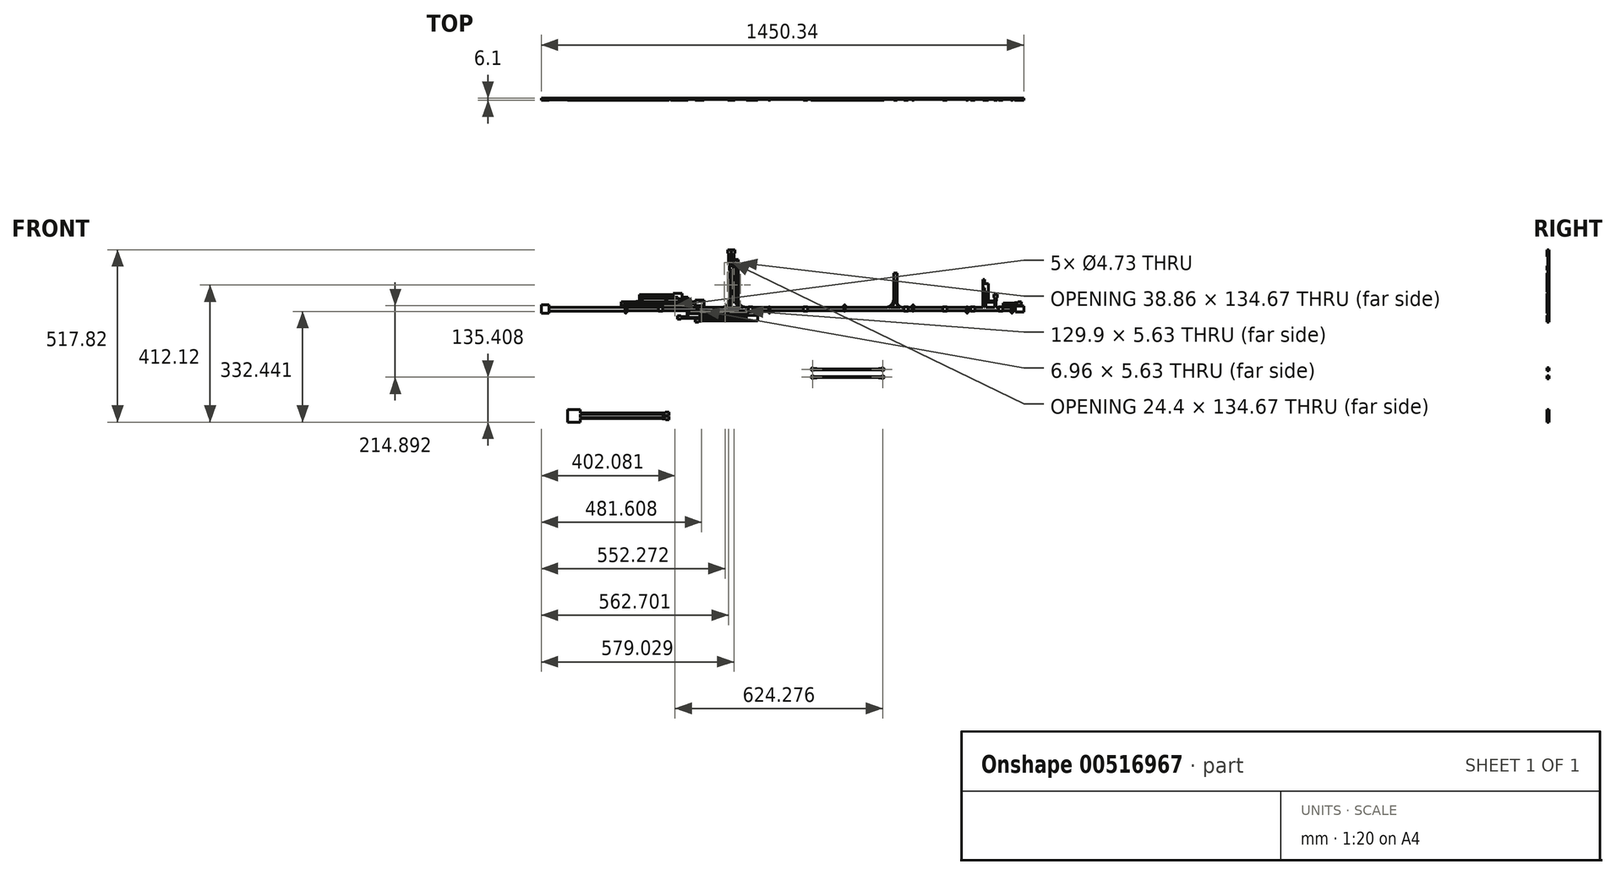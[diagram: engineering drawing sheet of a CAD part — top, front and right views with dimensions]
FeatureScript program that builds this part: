
annotation { "Feature Type Name" : "Feature", "Feature Type Description" : "" }
export const myFeature = defineFeature(function(context is Context, id is Id, definition is map)
    precondition{}
    {
        {
            var Q0;
            Q0=qCreatedBy(makeId("Front.planeOp"),FACE);
            var sketch = newSketch(context, id + "F0", { "sketchPlane" : qUnion([Q0])});
            skLineSegment(sketch, "E0.bottom", {"start": v(-1284.8, 12.7) * mm, "end": v(-1261.94, 12.7) * mm});
            skLineSegment(sketch, "E0.top", {"start": v(-1284.8, -12.7) * mm, "end": v(-1261.94, -12.7) * mm});
            skLineSegment(sketch, "E0.left", {"start": v(-1284.8, 12.7) * mm, "end": v(-1284.8, -12.7) * mm});
            skLineSegment(sketch, "E0.right", {"start": v(-1261.94, 12.7) * mm, "end": v(-1261.94, -12.7) * mm});
            skPoint(sketch, "E0.middle", {"position": v(-1273.37, 0) * mm});
            skLineSegment(sketch, "E1", {"start": v(-1273.37, 0) * mm, "end": v(152.84, 0) * mm, "construction": true});
            skLineSegment(sketch, "E2.bottom", {"start": v(140.14, 8.38) * mm, "end": v(165.54, 8.38) * mm});
            skLineSegment(sketch, "E2.top", {"start": v(140.14, -8.38) * mm, "end": v(165.54, -8.38) * mm});
            skLineSegment(sketch, "E2.left", {"start": v(140.14, 8.38) * mm, "end": v(140.14, -8.38) * mm});
            skLineSegment(sketch, "E2.right", {"start": v(165.54, 8.38) * mm, "end": v(165.54, -8.38) * mm});
            skPoint(sketch, "E2.middle", {"position": v(152.84, 0) * mm});
            skLineSegment(sketch, "E3.bottom", {"start": v(-795.85, 9.73) * mm, "end": v(-822.52, 9.73) * mm});
            skLineSegment(sketch, "E3.top", {"start": v(-795.85, 26.5) * mm, "end": v(-822.52, 26.5) * mm});
            skLineSegment(sketch, "E3.left", {"start": v(-795.85, 9.73) * mm, "end": v(-795.85, 26.5) * mm});
            skLineSegment(sketch, "E3.right", {"start": v(-822.52, 9.73) * mm, "end": v(-822.52, 26.5) * mm});
            skPoint(sketch, "E3.middle", {"position": v(-809.19, 18.11) * mm});
            skLineSegment(sketch, "E4.bottom", {"start": v(-861.64, 35.7) * mm, "end": v(-888.05, 35.7) * mm});
            skLineSegment(sketch, "E4.top", {"start": v(-861.64, 47.38) * mm, "end": v(-888.05, 47.38) * mm});
            skLineSegment(sketch, "E4.left", {"start": v(-861.64, 35.7) * mm, "end": v(-861.64, 47.38) * mm});
            skLineSegment(sketch, "E4.right", {"start": v(-888.05, 35.7) * mm, "end": v(-888.05, 47.38) * mm});
            skPoint(sketch, "E4.middle", {"position": v(-874.85, 41.54) * mm});
            skLineSegment(sketch, "E5.bottom", {"start": v(-874.08, 35.7) * mm, "end": v(-844.11, 35.7) * mm});
            skLineSegment(sketch, "E5.top", {"start": v(-874.08, 30.62) * mm, "end": v(-844.11, 30.62) * mm});
            skLineSegment(sketch, "E5.left", {"start": v(-874.08, 35.7) * mm, "end": v(-874.08, 30.62) * mm});
            skLineSegment(sketch, "E5.right", {"start": v(-844.11, 35.7) * mm, "end": v(-844.11, 30.62) * mm});
            skArc(sketch, "E6", {"start": v(-886.53, 8.25) * mm, "mid": v(-878.4, 10.28) * mm, "end": v(-886.53, 12.31) * mm});
            skCircle(sketch, "E7", {"center": v(-882.72, 10.28) * mm, "radius": 2.36 * mm});
            skLineSegment(sketch, "E8.bottom", {"start": v(-886.53, 12.31) * mm, "end": v(-895.17, 12.31) * mm});
            skLineSegment(sketch, "E8.top", {"start": v(-886.53, 8.25) * mm, "end": v(-895.17, 8.25) * mm});
            skLineSegment(sketch, "E8.right", {"start": v(-895.17, 12.31) * mm, "end": v(-895.17, 8.25) * mm});
            skLineSegment(sketch, "E9.bottom", {"start": v(-1032.58, 6.35) * mm, "end": v(-1029.02, 6.35) * mm});
            skLineSegment(sketch, "E9.top", {"start": v(-1032.61, -6.35) * mm, "end": v(-1029.06, -6.35) * mm});
            skLineSegment(sketch, "E9.right", {"start": v(-1029.02, 6.35) * mm, "end": v(-1029.06, -6.35) * mm});
            skPoint(sketch, "E9.middle", {"position": v(-1030.82, 0) * mm});
            skLineSegment(sketch, "E10", {"start": v(-1032.58, 6.35) * mm, "end": v(-1032.61, -6.35) * mm});
            skCircle(sketch, "E11", {"center": v(-1030.83, -8.98) * mm, "radius": 3.18 * mm});
            skPoint(sketch, "E12", {"position": v(-1030.8, 6.35) * mm});
            skPoint(sketch, "E13", {"position": v(-895.17, 10.28) * mm});
            skLineSegment(sketch, "E14", {"start": v(-1261.94, 6.35) * mm, "end": v(140.14, 6.35) * mm, "construction": true});
            skLineSegment(sketch, "E15", {"start": v(-1261.94, -6.35) * mm, "end": v(140.14, -6.35) * mm, "construction": true});
            skLineSegment(sketch, "E16", {"start": v(-1240.29, 6.35) * mm, "end": v(-1240.29, -6.35) * mm, "construction": true});
            skPoint(sketch, "E17", {"position": v(-1240.29, 0) * mm});
            skLineSegment(sketch, "E18.bottom", {"start": v(-932, 6.35) * mm, "end": v(-919.3, 6.35) * mm});
            skLineSegment(sketch, "E18.top", {"start": v(-932, -6.35) * mm, "end": v(-919.3, -6.35) * mm});
            skLineSegment(sketch, "E18.left", {"start": v(-932, 6.35) * mm, "end": v(-932, -6.35) * mm});
            skLineSegment(sketch, "E18.right", {"start": v(-919.3, 6.35) * mm, "end": v(-919.3, -6.35) * mm});
            skLineSegment(sketch, "E19.right", {"start": v(-813.12, 6.35) * mm, "end": v(-813.12, -6.35) * mm});
            skLineSegment(sketch, "E20", {"start": v(-816.68, 6.35) * mm, "end": v(-816.68, -6.35) * mm});
            skCircle(sketch, "E21", {"center": v(-814.9, -8.98) * mm, "radius": 3.18 * mm});
            skLineSegment(sketch, "E22", {"start": v(-813.12, 6.35) * mm, "end": v(-816.68, 6.35) * mm});
            skPoint(sketch, "E23", {"position": v(-814.9, 6.35) * mm});
            skLineSegment(sketch, "E24.1.0.0", {"start": v(-600.78, 6.35) * mm, "end": v(-600.78, -6.35) * mm});
            skLineSegment(sketch, "E24.1.0.1", {"start": v(-597.22, 6.35) * mm, "end": v(-597.22, -6.35) * mm});
            skCircle(sketch, "E24.1.0.2", {"center": v(-599, -8.98) * mm, "radius": 3.18 * mm});
            skLineSegment(sketch, "E24.direction1", {"start": v(-814.9, -8.98) * mm, "end": v(-599, -8.98) * mm, "construction": true});
            skLineSegment(sketch, "E25", {"start": v(-600.78, 6.35) * mm, "end": v(-597.22, 6.35) * mm});
            skLineSegment(sketch, "E26.bottom", {"start": v(-668.6, -19.14) * mm, "end": v(-634.56, -19.14) * mm});
            skLineSegment(sketch, "E26.top", {"start": v(-668.6, -34.89) * mm, "end": v(-634.56, -34.89) * mm});
            skLineSegment(sketch, "E26.left", {"start": v(-668.6, -19.14) * mm, "end": v(-668.6, -34.89) * mm});
            skLineSegment(sketch, "E26.right", {"start": v(-634.56, -19.14) * mm, "end": v(-634.56, -34.89) * mm});
            skLineSegment(sketch, "E27.bottom", {"start": v(-822.52, -28.63) * mm, "end": v(-812.36, -28.63) * mm});
            skLineSegment(sketch, "E27.top", {"start": v(-822.52, -38.79) * mm, "end": v(-812.36, -38.79) * mm});
            skLineSegment(sketch, "E27.left", {"start": v(-822.52, -28.63) * mm, "end": v(-822.52, -38.79) * mm});
            skLineSegment(sketch, "E27.right", {"start": v(-812.36, -28.63) * mm, "end": v(-812.36, -38.79) * mm});
            skLineSegment(sketch, "E28.bottom", {"start": v(-812.36, -31.17) * mm, "end": v(-802.2, -31.17) * mm});
            skLineSegment(sketch, "E28.top", {"start": v(-812.36, -36.25) * mm, "end": v(-802.2, -36.25) * mm});
            skLineSegment(sketch, "E28.left", {"start": v(-812.36, -31.17) * mm, "end": v(-812.36, -36.25) * mm});
            skLineSegment(sketch, "E28.right", {"start": v(-802.2, -31.17) * mm, "end": v(-802.2, -36.25) * mm});
            skPoint(sketch, "E29", {"position": v(-812.36, -33.7) * mm});
            skLineSegment(sketch, "E30.bottom", {"start": v(-875.86, -19.87) * mm, "end": v(-865.7, -19.87) * mm});
            skLineSegment(sketch, "E30.top", {"start": v(-875.86, -30.03) * mm, "end": v(-865.7, -30.03) * mm});
            skLineSegment(sketch, "E30.left", {"start": v(-875.86, -19.87) * mm, "end": v(-875.86, -30.03) * mm});
            skLineSegment(sketch, "E30.right", {"start": v(-865.7, -19.87) * mm, "end": v(-865.7, -30.03) * mm});
            skLineSegment(sketch, "E31.bottom", {"start": v(-865.7, -22.41) * mm, "end": v(-855.54, -22.41) * mm});
            skLineSegment(sketch, "E31.top", {"start": v(-865.7, -27.5) * mm, "end": v(-855.54, -27.5) * mm});
            skLineSegment(sketch, "E31.left", {"start": v(-865.7, -22.41) * mm, "end": v(-865.7, -27.5) * mm});
            skLineSegment(sketch, "E31.right", {"start": v(-855.54, -22.41) * mm, "end": v(-855.54, -27.5) * mm});
            skPoint(sketch, "E32", {"position": v(-865.7, -24.95) * mm});
            skLineSegment(sketch, "E33.bottom", {"start": v(-662.5, 6.35) * mm, "end": v(-649.8, 6.35) * mm});
            skLineSegment(sketch, "E33.top", {"start": v(-662.5, -8.98) * mm, "end": v(-649.8, -8.98) * mm});
            skLineSegment(sketch, "E33.left", {"start": v(-662.5, 6.35) * mm, "end": v(-662.5, -8.98) * mm});
            skLineSegment(sketch, "E33.right", {"start": v(-649.8, 6.35) * mm, "end": v(-649.8, -8.98) * mm});
            skPoint(sketch, "E34", {"position": v(-599, 6.35) * mm});
            skLineSegment(sketch, "E35.bottom", {"start": v(-724.32, 177.8) * mm, "end": v(-714.16, 177.8) * mm});
            skLineSegment(sketch, "E35.top", {"start": v(-724.32, 167.64) * mm, "end": v(-714.16, 167.64) * mm});
            skLineSegment(sketch, "E35.left", {"start": v(-724.32, 177.8) * mm, "end": v(-724.32, 167.64) * mm});
            skLineSegment(sketch, "E35.right", {"start": v(-714.16, 177.8) * mm, "end": v(-714.16, 167.64) * mm});
            skLineSegment(sketch, "E36.bottom", {"start": v(-716.7, 167.64) * mm, "end": v(-721.78, 167.64) * mm});
            skLineSegment(sketch, "E36.top", {"start": v(-716.7, 157.48) * mm, "end": v(-721.78, 157.48) * mm});
            skLineSegment(sketch, "E36.left", {"start": v(-716.7, 167.64) * mm, "end": v(-716.7, 157.48) * mm});
            skLineSegment(sketch, "E36.right", {"start": v(-721.78, 167.64) * mm, "end": v(-721.78, 157.48) * mm});
            skPoint(sketch, "E37", {"position": v(-719.24, 167.64) * mm});
            skLineSegment(sketch, "E38", {"start": v(-713.3, 0) * mm, "end": v(-713.3, 177.8) * mm, "construction": true});
            skLineSegment(sketch, "E39.MirrorCS", {"start": v(-702.28, 167.64) * mm, "end": v(-712.44, 167.64) * mm});
            skLineSegment(sketch, "E40.MirrorCS", {"start": v(-709.9, 167.64) * mm, "end": v(-704.82, 167.64) * mm});
            skPoint(sketch, "E41.MirrorP", {"position": v(-707.36, 167.64) * mm});
            skLineSegment(sketch, "E42.MirrorCS", {"start": v(-712.44, 177.8) * mm, "end": v(-712.44, 167.64) * mm});
            skLineSegment(sketch, "E43.MirrorCS", {"start": v(-702.28, 177.8) * mm, "end": v(-712.44, 177.8) * mm});
            skLineSegment(sketch, "E44.MirrorCS", {"start": v(-709.9, 157.48) * mm, "end": v(-704.82, 157.48) * mm});
            skLineSegment(sketch, "E45.MirrorCS", {"start": v(-702.28, 177.8) * mm, "end": v(-702.28, 167.64) * mm});
            skLineSegment(sketch, "E46.MirrorCS", {"start": v(-709.9, 167.64) * mm, "end": v(-709.9, 157.48) * mm});
            skLineSegment(sketch, "E47.MirrorCS", {"start": v(-704.82, 167.64) * mm, "end": v(-704.82, 157.48) * mm});
            skLineSegment(sketch, "E48.bottom", {"start": v(-719.65, 130.18) * mm, "end": v(-706.95, 130.18) * mm});
            skLineSegment(sketch, "E48.top", {"start": v(-719.65, 117.48) * mm, "end": v(-706.95, 117.48) * mm});
            skLineSegment(sketch, "E48.left", {"start": v(-719.65, 130.18) * mm, "end": v(-719.65, 117.48) * mm});
            skLineSegment(sketch, "E48.right", {"start": v(-706.95, 130.18) * mm, "end": v(-706.95, 117.48) * mm});
            skPoint(sketch, "E49", {"position": v(-713.3, 117.48) * mm});
            skLineSegment(sketch, "E50.bottom", {"start": v(-716.7, 157.48) * mm, "end": v(-719.65, 157.48) * mm});
            skLineSegment(sketch, "E50.top", {"start": v(-716.7, 100.8) * mm, "end": v(-719.65, 100.8) * mm, "construction": true});
            skLineSegment(sketch, "E50.left", {"start": v(-716.7, 157.48) * mm, "end": v(-716.7, 100.8) * mm, "construction": true});
            skLineSegment(sketch, "E50.right", {"start": v(-719.65, 157.48) * mm, "end": v(-719.65, 100.8) * mm, "construction": true});
            skLineSegment(sketch, "E51.bottom", {"start": v(-709.9, 157.48) * mm, "end": v(-706.95, 157.48) * mm});
            skLineSegment(sketch, "E51.top", {"start": v(-709.9, 98.87) * mm, "end": v(-706.95, 98.87) * mm, "construction": true});
            skLineSegment(sketch, "E51.left", {"start": v(-709.9, 157.48) * mm, "end": v(-709.9, 98.87) * mm, "construction": true});
            skLineSegment(sketch, "E51.right", {"start": v(-706.95, 157.48) * mm, "end": v(-706.95, 98.87) * mm, "construction": true});
            skLineSegment(sketch, "E52.1.0.0", {"start": v(-374.72, 6.35) * mm, "end": v(-374.72, -6.35) * mm});
            skLineSegment(sketch, "E52.1.0.1", {"start": v(-371.16, 6.35) * mm, "end": v(-371.16, -6.35) * mm});
            skLineSegment(sketch, "E52.direction1", {"start": v(-599, -8.98) * mm, "end": v(-372.94, -8.98) * mm, "construction": true});
            skLineSegment(sketch, "E53", {"start": v(-374.72, 6.35) * mm, "end": v(-371.16, 6.35) * mm});
            skLineSegment(sketch, "E54.bottom", {"start": v(-497.4, 6.35) * mm, "end": v(-484.7, 6.35) * mm});
            skLineSegment(sketch, "E54.top", {"start": v(-497.4, -6.35) * mm, "end": v(-484.7, -6.35) * mm});
            skLineSegment(sketch, "E54.left", {"start": v(-497.4, 6.35) * mm, "end": v(-497.4, -6.35) * mm});
            skLineSegment(sketch, "E54.right", {"start": v(-484.7, 6.35) * mm, "end": v(-484.7, -6.35) * mm});
            skLineSegment(sketch, "E55.1.0.0", {"start": v(-168.98, 6.35) * mm, "end": v(-168.98, -6.35) * mm});
            skLineSegment(sketch, "E55.1.0.1", {"start": v(-165.42, 6.35) * mm, "end": v(-165.42, -6.35) * mm});
            skLineSegment(sketch, "E55.direction1", {"start": v(-372.94, -8.98) * mm, "end": v(-167.2, -8.98) * mm, "construction": true});
            skLineSegment(sketch, "E56", {"start": v(-168.98, 6.35) * mm, "end": v(-165.42, 6.35) * mm});
            skLineSegment(sketch, "E57.1.0.0", {"start": v(-6.42, 6.35) * mm, "end": v(-6.42, -6.35) * mm});
            skLineSegment(sketch, "E57.1.0.1", {"start": v(-2.86, 6.35) * mm, "end": v(-2.86, -6.35) * mm});
            skCircle(sketch, "E57.1.0.2", {"center": v(-4.64, -8.98) * mm, "radius": 3.18 * mm});
            skLineSegment(sketch, "E57.direction1", {"start": v(-168.98, -6.35) * mm, "end": v(-6.42, -6.35) * mm, "construction": true});
            skLineSegment(sketch, "E58", {"start": v(-6.42, 6.35) * mm, "end": v(-2.86, 6.35) * mm});
            skLineSegment(sketch, "E59.bottom", {"start": v(-195.14, 6.35) * mm, "end": v(-182.44, 6.35) * mm});
            skLineSegment(sketch, "E59.top", {"start": v(-195.14, -6.35) * mm, "end": v(-182.44, -6.35) * mm});
            skLineSegment(sketch, "E59.left", {"start": v(-195.14, 6.35) * mm, "end": v(-195.14, -6.35) * mm});
            skLineSegment(sketch, "E59.right", {"start": v(-182.44, 6.35) * mm, "end": v(-182.44, -6.35) * mm});
            skLineSegment(sketch, "E60.bottom", {"start": v(-78.3, 6.35) * mm, "end": v(-65.6, 6.35) * mm});
            skLineSegment(sketch, "E60.top", {"start": v(-78.3, -6.35) * mm, "end": v(-65.6, -6.35) * mm});
            skLineSegment(sketch, "E60.left", {"start": v(-78.3, 6.35) * mm, "end": v(-78.3, -6.35) * mm});
            skLineSegment(sketch, "E60.right", {"start": v(-65.6, 6.35) * mm, "end": v(-65.6, -6.35) * mm});
            skLineSegment(sketch, "E61.bottom", {"start": v(5.52, 6.35) * mm, "end": v(18.22, 6.35) * mm});
            skLineSegment(sketch, "E61.top", {"start": v(5.52, -6.35) * mm, "end": v(18.22, -6.35) * mm});
            skLineSegment(sketch, "E61.left", {"start": v(5.52, 6.35) * mm, "end": v(5.52, -6.35) * mm});
            skLineSegment(sketch, "E61.right", {"start": v(18.22, 6.35) * mm, "end": v(18.22, -6.35) * mm});
            skLineSegment(sketch, "E62.bottom", {"start": v(89.34, 6.35) * mm, "end": v(102.04, 6.35) * mm});
            skLineSegment(sketch, "E62.top", {"start": v(89.34, -6.35) * mm, "end": v(102.04, -6.35) * mm});
            skLineSegment(sketch, "E62.left", {"start": v(89.34, 6.35) * mm, "end": v(89.34, -6.35) * mm});
            skLineSegment(sketch, "E62.right", {"start": v(102.04, 6.35) * mm, "end": v(102.04, -6.35) * mm});
            skCircle(sketch, "E63.1.0.0", {"center": v(129.98, -8.98) * mm, "radius": 3.18 * mm});
            skLineSegment(sketch, "E63.1.0.1", {"start": v(128.2, 6.35) * mm, "end": v(128.2, -6.35) * mm});
            skLineSegment(sketch, "E63.1.0.2", {"start": v(131.76, 6.35) * mm, "end": v(131.76, -6.35) * mm});
            skLineSegment(sketch, "E63.direction1", {"start": v(-4.64, -8.98) * mm, "end": v(129.98, -8.98) * mm, "construction": true});
            skLineSegment(sketch, "E64", {"start": v(128.2, 6.35) * mm, "end": v(131.76, 6.35) * mm});
            skLineSegment(sketch, "E65", {"start": v(-220.54, 6.35) * mm, "end": v(-220.54, 96.14) * mm, "construction": true});
            skLineSegment(sketch, "E66.bottom", {"start": v(-225.62, 107.95) * mm, "end": v(-215.46, 107.95) * mm});
            skLineSegment(sketch, "E66.top", {"start": v(-225.62, 84.33) * mm, "end": v(-215.46, 84.33) * mm});
            skLineSegment(sketch, "E66.left", {"start": v(-225.62, 107.95) * mm, "end": v(-225.62, 84.33) * mm});
            skLineSegment(sketch, "E66.right", {"start": v(-215.46, 107.95) * mm, "end": v(-215.46, 84.33) * mm});
            skPoint(sketch, "E66.middle", {"position": v(-220.54, 96.14) * mm});
            skLineSegment(sketch, "E67.bottom", {"start": v(147.76, 21.08) * mm, "end": v(157.92, 21.08) * mm});
            skLineSegment(sketch, "E67.top", {"start": v(147.76, 10.92) * mm, "end": v(157.92, 10.92) * mm});
            skLineSegment(sketch, "E67.left", {"start": v(147.76, 21.08) * mm, "end": v(147.76, 10.92) * mm});
            skLineSegment(sketch, "E67.right", {"start": v(157.92, 21.08) * mm, "end": v(157.92, 10.92) * mm});
            skLineSegment(sketch, "E68.bottom", {"start": v(147.76, 18.54) * mm, "end": v(137.6, 18.54) * mm});
            skLineSegment(sketch, "E68.top", {"start": v(147.76, 13.46) * mm, "end": v(137.6, 13.46) * mm});
            skLineSegment(sketch, "E68.left", {"start": v(147.76, 18.54) * mm, "end": v(147.76, 13.46) * mm});
            skLineSegment(sketch, "E68.right", {"start": v(137.6, 18.54) * mm, "end": v(137.6, 13.46) * mm});
            skLineSegment(sketch, "E69.bottom", {"start": v(75.37, 44.45) * mm, "end": v(85.53, 44.45) * mm});
            skLineSegment(sketch, "E69.top", {"start": v(75.37, 34.3) * mm, "end": v(85.53, 34.3) * mm});
            skLineSegment(sketch, "E69.left", {"start": v(75.37, 44.45) * mm, "end": v(75.37, 34.3) * mm});
            skLineSegment(sketch, "E69.right", {"start": v(85.53, 44.45) * mm, "end": v(85.53, 34.3) * mm});
            skLineSegment(sketch, "E70.bottom", {"start": v(77.9, 34.3) * mm, "end": v(82.99, 34.3) * mm});
            skLineSegment(sketch, "E70.top", {"start": v(77.9, 24.13) * mm, "end": v(82.99, 24.13) * mm});
            skLineSegment(sketch, "E70.left", {"start": v(77.9, 34.3) * mm, "end": v(77.9, 24.13) * mm});
            skLineSegment(sketch, "E70.right", {"start": v(82.99, 34.3) * mm, "end": v(82.99, 24.13) * mm});
            skLineSegment(sketch, "E71.bottom", {"start": v(47.43, 76.2) * mm, "end": v(58.86, 76.2) * mm});
            skLineSegment(sketch, "E71.top", {"start": v(47.43, 50.8) * mm, "end": v(58.86, 50.8) * mm});
            skLineSegment(sketch, "E71.left", {"start": v(47.43, 76.2) * mm, "end": v(47.43, 50.8) * mm});
            skLineSegment(sketch, "E71.right", {"start": v(58.86, 76.2) * mm, "end": v(58.86, 50.8) * mm});
            skPoint(sketch, "E72", {"position": v(80.45, 34.3) * mm});
            skPoint(sketch, "E73", {"position": v(147.76, 16) * mm});
            skLineSegment(sketch, "E74.bottom", {"start": v(42.35, 88.9) * mm, "end": v(47.43, 88.9) * mm});
            skLineSegment(sketch, "E74.top", {"start": v(42.35, 63.5) * mm, "end": v(47.43, 63.5) * mm});
            skLineSegment(sketch, "E74.left", {"start": v(42.35, 88.9) * mm, "end": v(42.35, 63.5) * mm});
            skLineSegment(sketch, "E74.right", {"start": v(47.43, 88.9) * mm, "end": v(47.43, 63.5) * mm});
            skCircle(sketch, "E75", {"center": v(-372.94, 8.98) * mm, "radius": 3.18 * mm});
            skLineSegment(sketch, "E76", {"start": v(-374.72, -6.35) * mm, "end": v(-371.16, -6.35) * mm});
            skLineSegment(sketch, "E77", {"start": v(-168.98, -6.35) * mm, "end": v(-165.42, -6.35) * mm});
            skCircle(sketch, "E78", {"center": v(-167.2, 8.98) * mm, "radius": 3.18 * mm});
            skArc(sketch, "E79", {"start": v(-262.25, -183.1) * mm, "mid": v(-254.13, -181.07) * mm, "end": v(-262.25, -179.04) * mm});
            skCircle(sketch, "E80", {"center": v(-258.44, -181.07) * mm, "radius": 2.36 * mm});
            skLineSegment(sketch, "E81.bottom", {"start": v(-262.25, -179.04) * mm, "end": v(-270.89, -179.04) * mm});
            skLineSegment(sketch, "E81.top", {"start": v(-262.25, -183.1) * mm, "end": v(-270.89, -183.1) * mm});
            skLineSegment(sketch, "E81.right", {"start": v(-270.89, -179.04) * mm, "end": v(-270.89, -183.1) * mm});
            skArc(sketch, "E82", {"start": v(-262.25, -206.64) * mm, "mid": v(-254.13, -204.61) * mm, "end": v(-262.25, -202.58) * mm});
            skCircle(sketch, "E83", {"center": v(-258.44, -204.61) * mm, "radius": 2.36 * mm});
            skLineSegment(sketch, "E84.bottom", {"start": v(-262.25, -202.58) * mm, "end": v(-270.89, -202.58) * mm});
            skLineSegment(sketch, "E84.top", {"start": v(-262.25, -206.64) * mm, "end": v(-270.89, -206.64) * mm});
            skLineSegment(sketch, "E84.right", {"start": v(-270.89, -202.58) * mm, "end": v(-270.89, -206.64) * mm});
            skLineSegment(sketch, "E85", {"start": v(-363.85, -66.24) * mm, "end": v(-363.85, -111.75) * mm, "construction": true});
            skLineSegment(sketch, "E86.bottom", {"start": v(-270.89, -182.34) * mm, "end": v(-363.85, -182.34) * mm});
            skLineSegment(sketch, "E86.top", {"start": v(-270.89, -180.49) * mm, "end": v(-363.85, -180.49) * mm});
            skLineSegment(sketch, "E86.left", {"start": v(-270.89, -180.49) * mm, "end": v(-270.89, -182.34) * mm});
            skLineSegment(sketch, "E86.right", {"start": v(-363.85, -180.49) * mm, "end": v(-363.85, -182.34) * mm});
            skLineSegment(sketch, "E87", {"start": v(-270.89, -183.1) * mm, "end": v(-270.89, -202.58) * mm, "construction": true});
            skLineSegment(sketch, "E88", {"start": v(194.55, -192.84) * mm, "end": v(-270.89, -192.84) * mm, "construction": true});
            skLineSegment(sketch, "E89.MirrorCS", {"start": v(-270.89, -205.2) * mm, "end": v(-363.85, -205.2) * mm});
            skLineSegment(sketch, "E90.MirrorCS", {"start": v(-270.89, -203.34) * mm, "end": v(-363.85, -203.34) * mm});
            skLineSegment(sketch, "E91.MirrorCS", {"start": v(-456.82, -179.04) * mm, "end": v(-456.82, -183.1) * mm});
            skLineSegment(sketch, "E92.MirrorCS", {"start": v(-456.82, -180.49) * mm, "end": v(-456.82, -182.34) * mm});
            skLineSegment(sketch, "E93.MirrorCS", {"start": v(-456.82, -202.58) * mm, "end": v(-456.82, -206.64) * mm});
            skLineSegment(sketch, "E94.MirrorCS", {"start": v(-456.82, -203.34) * mm, "end": v(-363.85, -203.34) * mm});
            skLineSegment(sketch, "E95.MirrorCS", {"start": v(-456.82, -205.2) * mm, "end": v(-363.85, -205.2) * mm});
            skCircle(sketch, "E96.MirrorC", {"center": v(-469.26, -181.07) * mm, "radius": 2.36 * mm});
            skArc(sketch, "E97.MirrorCS", {"start": v(-465.45, -183.1) * mm, "mid": v(-473.58, -181.07) * mm, "end": v(-465.45, -179.04) * mm});
            skLineSegment(sketch, "E98.MirrorCS", {"start": v(-465.45, -202.58) * mm, "end": v(-456.82, -202.58) * mm});
            skLineSegment(sketch, "E99.MirrorCS", {"start": v(-456.82, -183.1) * mm, "end": v(-456.82, -202.58) * mm, "construction": true});
            skLineSegment(sketch, "E100.MirrorCS", {"start": v(-456.82, -180.49) * mm, "end": v(-363.85, -180.49) * mm});
            skLineSegment(sketch, "E101.MirrorCS", {"start": v(-456.82, -182.34) * mm, "end": v(-363.85, -182.34) * mm});
            skLineSegment(sketch, "E102.MirrorCS", {"start": v(-465.45, -206.64) * mm, "end": v(-456.82, -206.64) * mm});
            skCircle(sketch, "E103.MirrorC", {"center": v(-469.26, -204.61) * mm, "radius": 2.36 * mm});
            skArc(sketch, "E104.MirrorCS", {"start": v(-465.45, -206.64) * mm, "mid": v(-473.58, -204.61) * mm, "end": v(-465.45, -202.58) * mm});
            skLineSegment(sketch, "E105.MirrorCS", {"start": v(-465.45, -183.1) * mm, "end": v(-456.82, -183.1) * mm});
            skLineSegment(sketch, "E106.MirrorCS", {"start": v(-465.45, -179.04) * mm, "end": v(-456.82, -179.04) * mm});
            skLineSegment(sketch, "E107.MirrorCS", {"start": v(-922.26, -192.84) * mm, "end": v(-456.82, -192.84) * mm, "construction": true});
            skLineSegment(sketch, "E108.bottom", {"start": v(-1205.08, -301.92) * mm, "end": v(-1166.98, -301.92) * mm});
            skLineSegment(sketch, "E108.top", {"start": v(-1205.08, -340.02) * mm, "end": v(-1166.98, -340.02) * mm});
            skLineSegment(sketch, "E108.left", {"start": v(-1205.08, -301.92) * mm, "end": v(-1205.08, -340.02) * mm});
            skLineSegment(sketch, "E108.right", {"start": v(-1166.98, -301.92) * mm, "end": v(-1166.98, -340.02) * mm});
            skLineSegment(sketch, "E109.bottom", {"start": v(-1166.98, -312.72) * mm, "end": v(-914.3, -312.72) * mm});
            skLineSegment(sketch, "E109.top", {"start": v(-1166.98, -315.9) * mm, "end": v(-914.3, -315.9) * mm});
            skLineSegment(sketch, "E109.left", {"start": v(-1166.98, -312.72) * mm, "end": v(-1166.98, -315.9) * mm});
            skLineSegment(sketch, "E109.right", {"start": v(-914.3, -312.72) * mm, "end": v(-914.3, -315.9) * mm});
            skLineSegment(sketch, "E110.bottom", {"start": v(-1166.98, -326.05) * mm, "end": v(-912.98, -326.05) * mm});
            skLineSegment(sketch, "E110.top", {"start": v(-1166.98, -329.23) * mm, "end": v(-912.98, -329.23) * mm});
            skLineSegment(sketch, "E110.left", {"start": v(-1166.98, -326.05) * mm, "end": v(-1166.98, -329.23) * mm});
            skLineSegment(sketch, "E110.right", {"start": v(-912.98, -326.05) * mm, "end": v(-912.98, -329.23) * mm});
            skPoint(sketch, "E111", {"position": v(-914.3, -314.3) * mm});
            skPoint(sketch, "E112", {"position": v(-912.98, -327.64) * mm});
            skLineSegment(sketch, "E113.bottom", {"start": v(-922.36, -311.77) * mm, "end": v(-906.24, -311.77) * mm});
            skLineSegment(sketch, "E113.top", {"start": v(-922.36, -316.85) * mm, "end": v(-906.24, -316.85) * mm});
            skLineSegment(sketch, "E113.left", {"start": v(-922.36, -311.77) * mm, "end": v(-922.36, -316.85) * mm});
            skLineSegment(sketch, "E113.right", {"start": v(-906.24, -311.77) * mm, "end": v(-906.24, -316.85) * mm});
            skLineSegment(sketch, "E114.bottom", {"start": v(-912.2, -309.23) * mm, "end": v(-900.28, -309.23) * mm});
            skLineSegment(sketch, "E114.top", {"start": v(-912.2, -319.39) * mm, "end": v(-900.28, -319.39) * mm});
            skLineSegment(sketch, "E114.left", {"start": v(-912.2, -309.23) * mm, "end": v(-912.2, -319.39) * mm});
            skLineSegment(sketch, "E114.right", {"start": v(-900.28, -309.23) * mm, "end": v(-900.28, -319.39) * mm});
            skPoint(sketch, "E114.middle", {"position": v(-906.24, -314.3) * mm});
            skLineSegment(sketch, "E115.bottom", {"start": v(-920.6, -325.1) * mm, "end": v(-905.36, -325.1) * mm});
            skLineSegment(sketch, "E115.top", {"start": v(-920.6, -330.18) * mm, "end": v(-905.36, -330.18) * mm});
            skLineSegment(sketch, "E115.left", {"start": v(-920.6, -325.1) * mm, "end": v(-920.6, -330.18) * mm});
            skLineSegment(sketch, "E115.right", {"start": v(-905.36, -325.1) * mm, "end": v(-905.36, -330.18) * mm});
            skLineSegment(sketch, "E116.bottom", {"start": v(-910.44, -322.56) * mm, "end": v(-900.28, -322.56) * mm});
            skLineSegment(sketch, "E116.top", {"start": v(-910.44, -332.72) * mm, "end": v(-900.28, -332.72) * mm});
            skLineSegment(sketch, "E116.left", {"start": v(-910.44, -322.56) * mm, "end": v(-910.44, -332.72) * mm});
            skLineSegment(sketch, "E116.right", {"start": v(-900.28, -322.56) * mm, "end": v(-900.28, -332.72) * mm});
            skPoint(sketch, "E116.middle", {"position": v(-905.36, -327.64) * mm});
            skLineSegment(sketch, "E117", {"start": v(-1045.91, -315.9) * mm, "end": v(-1045.91, -326.05) * mm, "construction": true});
            skPoint(sketch, "E118", {"position": v(-1045.91, -320.97) * mm});
            skPoint(sketch, "E119", {"position": v(-1166.98, -320.97) * mm});
            skLineSegment(sketch, "E120", {"start": v(-1166.98, -320.97) * mm, "end": v(-1045.91, -320.97) * mm, "construction": true});
            skSolve(sketch);
        }
        {
            var Q0;
            Q0 = qSketchRegion(id + "F0", true);
            extrude(context, id + "F1", {"entities" : qUnion([Q0]), "depth" : 6.1 * mm, "offsetDistance" : 25.4 * mm});
        }
        {
            var Q0;
            Q0=qCreatedBy(makeId("Front.planeOp"),FACE);
            var sketch = newSketch(context, id + "F2", { "sketchPlane" : qUnion([Q0])});
            skLineSegment(sketch, "E121.bottom", {"start": v(-1261.94, 4.76) * mm, "end": v(-743.83, 4.76) * mm});
            skLineSegment(sketch, "E121.top", {"start": v(-1261.94, -4.76) * mm, "end": v(-810.7, -4.76) * mm});
            skLineSegment(sketch, "E121.left", {"start": v(-1261.94, 4.76) * mm, "end": v(-1261.94, -4.76) * mm});
            skLineSegment(sketch, "E121.right", {"start": v(140.14, 4.76) * mm, "end": v(140.14, -4.76) * mm});
            skPoint(sketch, "E122.0", {"position": v(-1261.94, 0) * mm});
            skPoint(sketch, "E123", {"position": v(140.14, 0) * mm});
            skLineSegment(sketch, "E124.bottom", {"start": v(-1044.74, 4.76) * mm, "end": v(-1038.32, 4.76) * mm});
            skLineSegment(sketch, "E124.top", {"start": v(-1044.74, 14.94) * mm, "end": v(-1038.32, 14.94) * mm});
            skLineSegment(sketch, "E124.left", {"start": v(-1044.74, 4.76) * mm, "end": v(-1044.74, 14.94) * mm});
            skLineSegment(sketch, "E124.right", {"start": v(-1038.32, 4.76) * mm, "end": v(-1038.32, 14.94) * mm});
            skLineSegment(sketch, "E125", {"start": v(-1025.72, 4.76) * mm, "end": v(-1025.72, 12.06) * mm});
            skLineSegment(sketch, "E126", {"start": v(-1025.72, 12.06) * mm, "end": v(-895.17, 12.06) * mm});
            skLineSegment(sketch, "E127", {"start": v(-895.17, 12.06) * mm, "end": v(-895.17, 8.5) * mm});
            skLineSegment(sketch, "E128", {"start": v(-895.17, 8.5) * mm, "end": v(-1022.17, 8.5) * mm});
            skLineSegment(sketch, "E129", {"start": v(-1022.17, 8.5) * mm, "end": v(-1022.17, 4.76) * mm});
            skPoint(sketch, "E130.0", {"position": v(-1030.8, 6.35) * mm});
            skPoint(sketch, "E131.0", {"position": v(-895.17, 10.28) * mm});
            skLineSegment(sketch, "E132.bottom", {"start": v(-1044.74, 14.94) * mm, "end": v(-822.52, 14.94) * mm});
            skLineSegment(sketch, "E132.top", {"start": v(-1044.74, 21.29) * mm, "end": v(-822.52, 21.29) * mm});
            skLineSegment(sketch, "E132.left", {"start": v(-1044.74, 14.94) * mm, "end": v(-1044.74, 21.29) * mm});
            skLineSegment(sketch, "E132.right", {"start": v(-822.52, 14.94) * mm, "end": v(-822.52, 17.99) * mm});
            skPoint(sketch, "E133", {"position": v(-822.52, 18.11) * mm});
            skLineSegment(sketch, "E134.bottom", {"start": v(-990.16, 21.29) * mm, "end": v(-986.6, 21.29) * mm});
            skLineSegment(sketch, "E134.top", {"start": v(-990.16, 39.76) * mm, "end": v(-986.6, 39.76) * mm});
            skLineSegment(sketch, "E134.left", {"start": v(-990.16, 21.29) * mm, "end": v(-990.16, 39.76) * mm});
            skLineSegment(sketch, "E134.right", {"start": v(-986.6, 21.29) * mm, "end": v(-986.6, 39.76) * mm});
            skLineSegment(sketch, "E135.bottom", {"start": v(-984.07, 21.29) * mm, "end": v(-980.5, 21.29) * mm});
            skLineSegment(sketch, "E135.top", {"start": v(-984.07, 31.38) * mm, "end": v(-980.5, 31.38) * mm});
            skLineSegment(sketch, "E135.left", {"start": v(-984.07, 21.29) * mm, "end": v(-984.07, 31.38) * mm});
            skLineSegment(sketch, "E135.right", {"start": v(-980.5, 21.29) * mm, "end": v(-980.5, 31.38) * mm});
            skLineSegment(sketch, "E136.bottom", {"start": v(-984.07, 31.38) * mm, "end": v(-874.08, 31.38) * mm});
            skLineSegment(sketch, "E136.top", {"start": v(-984.07, 34.94) * mm, "end": v(-874.08, 34.94) * mm});
            skLineSegment(sketch, "E136.left", {"start": v(-984.07, 31.38) * mm, "end": v(-984.07, 34.94) * mm});
            skLineSegment(sketch, "E136.right", {"start": v(-874.08, 31.38) * mm, "end": v(-874.08, 34.94) * mm});
            skLineSegment(sketch, "E137.bottom", {"start": v(-990.16, 39.76) * mm, "end": v(-888.05, 39.76) * mm});
            skLineSegment(sketch, "E137.top", {"start": v(-990.16, 43.32) * mm, "end": v(-888.05, 43.32) * mm});
            skLineSegment(sketch, "E137.left", {"start": v(-990.16, 39.76) * mm, "end": v(-990.16, 43.32) * mm});
            skLineSegment(sketch, "E137.right", {"start": v(-888.05, 39.76) * mm, "end": v(-888.05, 43.32) * mm});
            skPoint(sketch, "E138", {"position": v(-888.05, 41.54) * mm});
            skPoint(sketch, "E139", {"position": v(-874.08, 33.16) * mm});
            skLineSegment(sketch, "E140.right", {"start": v(-668.6, -18.83) * mm, "end": v(-668.6, -21.32) * mm});
            skLineSegment(sketch, "E141.bottom", {"start": v(-802.2, -32.1) * mm, "end": v(-668.6, -32.1) * mm});
            skLineSegment(sketch, "E141.top", {"start": v(-802.2, -35.32) * mm, "end": v(-668.6, -35.32) * mm});
            skLineSegment(sketch, "E141.left", {"start": v(-802.2, -32.1) * mm, "end": v(-802.2, -35.32) * mm});
            skLineSegment(sketch, "E141.right", {"start": v(-668.6, -32.1) * mm, "end": v(-668.6, -35.32) * mm});
            skPoint(sketch, "E142.0", {"position": v(-802.2, -33.7) * mm});
            skPoint(sketch, "E143.oppositeSnap0", {"position": v(-1041.53, 14.94) * mm});
            skLineSegment(sketch, "E143.bottom", {"start": v(-1078.55, 4.76) * mm, "end": v(-1077.47, 4.76) * mm});
            skLineSegment(sketch, "E144.bottom", {"start": v(-984.07, 18.24) * mm, "end": v(-822.52, 18.24) * mm});
            skLineSegment(sketch, "E144.top", {"start": v(-984.07, 17.99) * mm, "end": v(-822.52, 17.99) * mm});
            skLineSegment(sketch, "E144.left", {"start": v(-984.07, 18.24) * mm, "end": v(-984.07, 17.99) * mm});
            skLineSegment(sketch, "E145.trimOffspring", {"start": v(-822.52, 18.24) * mm, "end": v(-822.52, 21.29) * mm});
            skLineSegment(sketch, "E146.bottom", {"start": v(-668.6, -22.8) * mm, "end": v(-668.62, -22.8) * mm});
            skLineSegment(sketch, "E146.top", {"start": v(-668.6, -32.1) * mm, "end": v(-668.62, -32.1) * mm});
            skLineSegment(sketch, "E146.left", {"start": v(-668.6, -22.8) * mm, "end": v(-668.6, -32.1) * mm});
            skLineSegment(sketch, "E146.right", {"start": v(-668.62, -22.8) * mm, "end": v(-668.62, -32.1) * mm});
            skLineSegment(sketch, "E147.bottom", {"start": v(-668.62, -25.59) * mm, "end": v(-855.54, -25.59) * mm});
            skLineSegment(sketch, "E147.top", {"start": v(-668.62, -27.5) * mm, "end": v(-855.54, -27.5) * mm});
            skLineSegment(sketch, "E147.left", {"start": v(-668.62, -25.59) * mm, "end": v(-668.62, -27.5) * mm});
            skLineSegment(sketch, "E147.right", {"start": v(-855.54, -25.59) * mm, "end": v(-855.54, -27.5) * mm});
            skLineSegment(sketch, "E148.bottom", {"start": v(-664.53, -4.76) * mm, "end": v(-667.58, -4.76) * mm});
            skLineSegment(sketch, "E148.top", {"start": v(-664.53, -13.44) * mm, "end": v(-667.58, -13.44) * mm});
            skLineSegment(sketch, "E148.left", {"start": v(-664.53, -4.76) * mm, "end": v(-664.53, -13.44) * mm});
            skLineSegment(sketch, "E148.right", {"start": v(-667.58, -4.76) * mm, "end": v(-667.58, -13.44) * mm});
            skLineSegment(sketch, "E149.bottom", {"start": v(-667.58, -13.44) * mm, "end": v(-846.47, -13.44) * mm});
            skLineSegment(sketch, "E149.top", {"start": v(-667.58, -10.4) * mm, "end": v(-846.47, -10.4) * mm});
            skLineSegment(sketch, "E149.left", {"start": v(-667.58, -10.4) * mm, "end": v(-667.58, -13.44) * mm});
            skLineSegment(sketch, "E149.right", {"start": v(-846.47, -10.4) * mm, "end": v(-846.47, -13.44) * mm});
            skLineSegment(sketch, "E150.bottom", {"start": v(-846.47, -13.44) * mm, "end": v(-843.43, -13.44) * mm});
            skLineSegment(sketch, "E150.top", {"start": v(-846.47, -24.32) * mm, "end": v(-843.43, -24.32) * mm});
            skLineSegment(sketch, "E150.left", {"start": v(-846.47, -13.44) * mm, "end": v(-846.47, -24.32) * mm});
            skLineSegment(sketch, "E150.right", {"start": v(-843.43, -13.44) * mm, "end": v(-843.43, -24.32) * mm});
            skLineSegment(sketch, "E151.bottom", {"start": v(-846.47, -24.32) * mm, "end": v(-855.54, -24.32) * mm});
            skLineSegment(sketch, "E151.top", {"start": v(-846.47, -22.41) * mm, "end": v(-855.54, -22.41) * mm});
            skLineSegment(sketch, "E151.left", {"start": v(-846.47, -24.32) * mm, "end": v(-846.47, -22.41) * mm});
            skLineSegment(sketch, "E151.right", {"start": v(-855.54, -24.32) * mm, "end": v(-855.54, -22.41) * mm});
            skLineSegment(sketch, "E152.bottom", {"start": v(-855.54, -22.41) * mm, "end": v(-855.57, -22.41) * mm});
            skLineSegment(sketch, "E152.top", {"start": v(-855.54, -27.5) * mm, "end": v(-855.57, -27.5) * mm});
            skLineSegment(sketch, "E152.left", {"start": v(-855.54, -22.41) * mm, "end": v(-855.54, -24.32) * mm});
            skPoint(sketch, "E153", {"position": v(-855.54, -24.95) * mm});
            skLineSegment(sketch, "E154.trimOffspring", {"start": v(-855.54, -24.95) * mm, "end": v(-855.54, -27.5) * mm});
            skLineSegment(sketch, "E155.top", {"start": v(-808.86, -21.44) * mm, "end": v(-808.74, -21.44) * mm});
            skPoint(sketch, "E156", {"position": v(-808.8, -4.76) * mm});
            skLineSegment(sketch, "E157.top", {"start": v(-799.71, -21.32) * mm, "end": v(-668.6, -21.32) * mm});
            skLineSegment(sketch, "E158.trimOffspring", {"start": v(-668.6, -21.44) * mm, "end": v(-668.6, -22.8) * mm});
            skLineSegment(sketch, "E159.trimOffspring", {"start": v(-808.86, -4.76) * mm, "end": v(-808.74, -4.76) * mm});
            skLineSegment(sketch, "E160.trimOffspring", {"start": v(-799.71, -18.83) * mm, "end": v(-668.6, -18.83) * mm});
            skLineSegment(sketch, "E161", {"start": v(-713.3, 4.76) * mm, "end": v(-713.3, 254.48) * mm, "construction": true});
            skLineSegment(sketch, "E162.0", {"start": v(-716.7, 157.48) * mm, "end": v(-721.78, 157.48) * mm, "construction": true});
            skLineSegment(sketch, "E163.0", {"start": v(-709.9, 157.48) * mm, "end": v(-704.82, 157.48) * mm, "construction": true});
            skPoint(sketch, "E164.0", {"position": v(-719.65, 130.18) * mm});
            skPoint(sketch, "E165.0", {"position": v(-706.95, 130.18) * mm});
            skLineSegment(sketch, "E166.bottom", {"start": v(-716.7, 157.48) * mm, "end": v(-718.43, 157.48) * mm});
            skLineSegment(sketch, "E166.top", {"start": v(-716.7, 4.76) * mm, "end": v(-719.65, 4.76) * mm});
            skLineSegment(sketch, "E166.left", {"start": v(-716.7, 157.48) * mm, "end": v(-716.7, 30.16) * mm});
            skLineSegment(sketch, "E166.right", {"start": v(-718.43, 157.48) * mm, "end": v(-718.43, 30.16) * mm});
            skLineSegment(sketch, "E167.bottom", {"start": v(-709.9, 157.48) * mm, "end": v(-707.97, 157.48) * mm});
            skLineSegment(sketch, "E167.top", {"start": v(-709.9, 4.76) * mm, "end": v(-706.95, 4.76) * mm});
            skLineSegment(sketch, "E167.left", {"start": v(-709.9, 157.48) * mm, "end": v(-709.9, 30.16) * mm});
            skLineSegment(sketch, "E167.right", {"start": v(-707.97, 157.48) * mm, "end": v(-707.97, 30.16) * mm});
            skArc(sketch, "E168", {"start": v(-743.83, 4.76) * mm, "mid": v(-725.87, 12.2) * mm, "end": v(-718.43, 30.16) * mm});
            skArc(sketch, "E169", {"start": v(-734.3, 4.76) * mm, "mid": v(-721.53, 14.71) * mm, "end": v(-716.7, 30.16) * mm});
            skArc(sketch, "E170", {"start": v(-734.01, 4.8) * mm, "mid": v(-716.89, 12.66) * mm, "end": v(-709.9, 30.16) * mm});
            skArc(sketch, "E171", {"start": v(-725.2, 4.76) * mm, "mid": v(-712.68, 14.81) * mm, "end": v(-707.97, 30.16) * mm});
            skLineSegment(sketch, "E172", {"start": v(-705.77, 4.76) * mm, "end": v(-705.77, 74.88) * mm, "construction": true});
            skArc(sketch, "E173.MirrorCS", {"start": v(-667.7, 4.76) * mm, "mid": v(-685.67, 12.2) * mm, "end": v(-693.1, 30.16) * mm});
            skArc(sketch, "E174.MirrorCS", {"start": v(-677.24, 4.76) * mm, "mid": v(-690, 14.71) * mm, "end": v(-694.84, 30.16) * mm});
            skArc(sketch, "E175.MirrorCS", {"start": v(-677.3, 4.78) * mm, "mid": v(-694.57, 12.58) * mm, "end": v(-701.64, 30.16) * mm});
            skArc(sketch, "E176.MirrorCS", {"start": v(-686.34, 4.76) * mm, "mid": v(-698.86, 14.81) * mm, "end": v(-703.58, 30.16) * mm});
            skLineSegment(sketch, "E177.MirrorCS", {"start": v(-703.58, 141.63) * mm, "end": v(-703.58, 30.16) * mm});
            skLineSegment(sketch, "E178.MirrorCS", {"start": v(-701.64, 141.63) * mm, "end": v(-701.64, 30.16) * mm});
            skLineSegment(sketch, "E179.MirrorCS", {"start": v(-694.84, 148.9) * mm, "end": v(-694.84, 30.16) * mm});
            skLineSegment(sketch, "E180.MirrorCS", {"start": v(-693.1, 148.9) * mm, "end": v(-693.1, 30.16) * mm});
            skLineSegment(sketch, "E181.bottom", {"start": v(-701.64, 139.44) * mm, "end": v(-721.78, 139.44) * mm});
            skLineSegment(sketch, "E181.top", {"start": v(-701.64, 141.63) * mm, "end": v(-721.78, 141.63) * mm});
            skLineSegment(sketch, "E181.left", {"start": v(-701.64, 139.44) * mm, "end": v(-701.64, 141.63) * mm});
            skLineSegment(sketch, "E181.right", {"start": v(-721.78, 139.44) * mm, "end": v(-721.78, 141.63) * mm});
            skLineSegment(sketch, "E182.bottom", {"start": v(-721.78, 141.63) * mm, "end": v(-720.2, 141.63) * mm});
            skLineSegment(sketch, "E182.top", {"start": v(-721.78, 157.48) * mm, "end": v(-720.2, 157.48) * mm});
            skLineSegment(sketch, "E182.left", {"start": v(-721.78, 141.63) * mm, "end": v(-721.78, 157.48) * mm});
            skLineSegment(sketch, "E182.right", {"start": v(-720.2, 141.63) * mm, "end": v(-720.2, 157.48) * mm});
            skPoint(sketch, "E183.orphan", {"position": v(-703.58, 157.48) * mm});
            skPoint(sketch, "E184.orphan", {"position": v(-701.64, 157.48) * mm});
            skLineSegment(sketch, "E185.bottom", {"start": v(-693.1, 148.9) * mm, "end": v(-704.82, 148.9) * mm});
            skLineSegment(sketch, "E185.top", {"start": v(-693.1, 147.18) * mm, "end": v(-704.82, 147.18) * mm});
            skLineSegment(sketch, "E185.left", {"start": v(-693.1, 147.18) * mm, "end": v(-693.1, 148.9) * mm});
            skLineSegment(sketch, "E185.right", {"start": v(-704.82, 147.18) * mm, "end": v(-704.82, 148.9) * mm});
            skLineSegment(sketch, "E186.bottom", {"start": v(-704.82, 147.18) * mm, "end": v(-706.5, 147.18) * mm});
            skLineSegment(sketch, "E186.top", {"start": v(-704.82, 157.48) * mm, "end": v(-706.5, 157.48) * mm});
            skLineSegment(sketch, "E186.left", {"start": v(-704.82, 147.18) * mm, "end": v(-704.82, 157.48) * mm});
            skLineSegment(sketch, "E186.right", {"start": v(-706.5, 147.18) * mm, "end": v(-706.5, 157.48) * mm});
            skPoint(sketch, "E187.orphan", {"position": v(-694.84, 157.48) * mm});
            skPoint(sketch, "E188.orphan", {"position": v(-693.1, 157.48) * mm});
            skLineSegment(sketch, "E189", {"start": v(-734.01, 4.8) * mm, "end": v(-734.01, 4.76) * mm});
            skPoint(sketch, "E190.orphan", {"position": v(-734.24, 4.78) * mm});
            skLineSegment(sketch, "E191.trimOffspring", {"start": v(-725.2, 4.76) * mm, "end": v(-251.02, 4.76) * mm});
            skLineSegment(sketch, "E192.trimOffspring", {"start": v(-734.3, 4.76) * mm, "end": v(-734.01, 4.76) * mm});
            skLineSegment(sketch, "E193.bottom", {"start": v(-716.7, 139.44) * mm, "end": v(-709.9, 139.44) * mm});
            skLineSegment(sketch, "E193.top", {"start": v(-716.7, 30.16) * mm, "end": v(-709.9, 30.16) * mm});
            skLineSegment(sketch, "E193.left", {"start": v(-716.7, 139.44) * mm, "end": v(-716.7, 30.16) * mm});
            skLineSegment(sketch, "E193.right", {"start": v(-709.9, 139.44) * mm, "end": v(-709.9, 30.16) * mm});
            skLineSegment(sketch, "E194.bottom", {"start": v(-799.71, -21.32) * mm, "end": v(-799.71, -18.83) * mm});
            skLineSegment(sketch, "E195.trimOffspring", {"start": v(-806.67, -4.76) * mm, "end": v(-799.71, -4.76) * mm});
            skLineSegment(sketch, "E196", {"start": v(-810.7, -22.8) * mm, "end": v(-810.39, -22.8) * mm});
            skPoint(sketch, "E197.0", {"position": v(-225.62, 84.33) * mm});
            skPoint(sketch, "E198.0", {"position": v(-215.46, 84.33) * mm});
            skLineSegment(sketch, "E199.bottom", {"start": v(-225.62, 84.33) * mm, "end": v(-223.61, 84.33) * mm});
            skLineSegment(sketch, "E199.left", {"start": v(-225.62, 84.33) * mm, "end": v(-225.62, 30.16) * mm});
            skLineSegment(sketch, "E199.right", {"start": v(-220.53, 84.33) * mm, "end": v(-220.53, 30.16) * mm});
            skLineSegment(sketch, "E200.bottom", {"start": v(-215.46, 84.33) * mm, "end": v(-217.8, 84.33) * mm});
            skLineSegment(sketch, "E200.top", {"start": v(-215.46, 23.81) * mm, "end": v(-217.8, 23.81) * mm});
            skLineSegment(sketch, "E200.left", {"start": v(-215.46, 84.33) * mm, "end": v(-215.46, 23.81) * mm});
            skLineSegment(sketch, "E200.right", {"start": v(-217.8, 84.33) * mm, "end": v(-217.8, 23.81) * mm});
            skArc(sketch, "E201", {"start": v(-251.02, 4.76) * mm, "mid": v(-233.06, 12.2) * mm, "end": v(-225.62, 30.16) * mm});
            skArc(sketch, "E202", {"start": v(-234.14, 4.76) * mm, "mid": v(-224.14, 15.75) * mm, "end": v(-220.53, 30.16) * mm});
            skLineSegment(sketch, "E203", {"start": v(-234.1, 11.23) * mm, "end": v(-230.7, 7.43) * mm, "construction": true});
            skLineSegment(sketch, "E204.left", {"start": v(-223.61, 84.33) * mm, "end": v(-223.61, 30.16) * mm});
            skLineSegment(sketch, "E204.right", {"start": v(-222.67, 84.33) * mm, "end": v(-222.67, 30.16) * mm});
            skArc(sketch, "E205", {"start": v(-240.73, 4.76) * mm, "mid": v(-228.3, 14.85) * mm, "end": v(-223.61, 30.16) * mm});
            skArc(sketch, "E206", {"start": v(-238.42, 4.76) * mm, "mid": v(-226.92, 15.22) * mm, "end": v(-222.67, 30.16) * mm});
            skLineSegment(sketch, "E207.trimOffspring", {"start": v(-240.73, 4.76) * mm, "end": v(-238.42, 4.76) * mm});
            skLineSegment(sketch, "E208.trimOffspring", {"start": v(-234.14, 4.76) * mm, "end": v(140.14, 4.76) * mm});
            skArc(sketch, "E209", {"start": v(-215.46, 23.81) * mm, "mid": v(-209.88, 10.34) * mm, "end": v(-196.41, 4.76) * mm});
            skArc(sketch, "E210", {"start": v(-217.8, 23.81) * mm, "mid": v(-207.58, 5.58) * mm, "end": v(-186.7, 4.76) * mm});
            skLineSegment(sketch, "E211.trimOffspring", {"start": v(-222.67, 84.33) * mm, "end": v(-220.53, 84.33) * mm});
            skLineSegment(sketch, "E212", {"start": v(103.81, 4.76) * mm, "end": v(103.81, 17.9) * mm});
            skLineSegment(sketch, "E213", {"start": v(103.81, 17.9) * mm, "end": v(137.6, 17.9) * mm});
            skLineSegment(sketch, "E214", {"start": v(137.6, 17.9) * mm, "end": v(137.6, 14.1) * mm});
            skLineSegment(sketch, "E215", {"start": v(137.6, 14.1) * mm, "end": v(107.62, 14.1) * mm});
            skLineSegment(sketch, "E216", {"start": v(107.62, 14.1) * mm, "end": v(107.62, 4.76) * mm});
            skPoint(sketch, "E217", {"position": v(137.6, 16) * mm});
            skLineSegment(sketch, "E218.bottom", {"start": v(78.54, 24.13) * mm, "end": v(82.35, 24.13) * mm});
            skLineSegment(sketch, "E218.top", {"start": v(78.54, 4.76) * mm, "end": v(82.35, 4.76) * mm});
            skLineSegment(sketch, "E218.left", {"start": v(78.54, 24.13) * mm, "end": v(78.54, 4.76) * mm});
            skLineSegment(sketch, "E218.right", {"start": v(82.35, 24.13) * mm, "end": v(82.35, 4.76) * mm});
            skPoint(sketch, "E219", {"position": v(80.45, 24.13) * mm});
            skLineSegment(sketch, "E220.bottom", {"start": v(78.54, 24.13) * mm, "end": v(58.86, 24.13) * mm});
            skLineSegment(sketch, "E220.top", {"start": v(78.54, 20.32) * mm, "end": v(58.86, 20.32) * mm});
            skLineSegment(sketch, "E220.left", {"start": v(78.54, 24.13) * mm, "end": v(78.54, 20.32) * mm});
            skLineSegment(sketch, "E220.right", {"start": v(58.86, 24.13) * mm, "end": v(58.86, 20.32) * mm});
            skLineSegment(sketch, "E221.bottom", {"start": v(58.86, 20.32) * mm, "end": v(55.05, 20.32) * mm});
            skLineSegment(sketch, "E221.top", {"start": v(58.86, 50.8) * mm, "end": v(55.05, 50.8) * mm});
            skLineSegment(sketch, "E221.left", {"start": v(58.86, 20.32) * mm, "end": v(58.86, 50.8) * mm});
            skLineSegment(sketch, "E221.right", {"start": v(55.05, 20.32) * mm, "end": v(55.05, 50.8) * mm});
            skPoint(sketch, "E222.0", {"position": v(58.86, 50.8) * mm});
            skPoint(sketch, "E223.0", {"position": v(47.43, 50.8) * mm});
            skPoint(sketch, "E224.0", {"position": v(42.35, 63.5) * mm});
            skLineSegment(sketch, "E225.bottom", {"start": v(42.35, 63.5) * mm, "end": v(46.16, 63.5) * mm});
            skLineSegment(sketch, "E225.top", {"start": v(42.35, 4.76) * mm, "end": v(46.16, 4.76) * mm});
            skLineSegment(sketch, "E225.left", {"start": v(42.35, 63.5) * mm, "end": v(42.35, 4.76) * mm});
            skLineSegment(sketch, "E225.right", {"start": v(46.16, 63.5) * mm, "end": v(46.16, 4.76) * mm});
            skLineSegment(sketch, "E226.bottom", {"start": v(47.43, 50.8) * mm, "end": v(51.24, 50.8) * mm});
            skLineSegment(sketch, "E226.top", {"start": v(47.43, 4.76) * mm, "end": v(51.24, 4.76) * mm});
            skLineSegment(sketch, "E226.left", {"start": v(47.43, 50.8) * mm, "end": v(47.43, 4.76) * mm});
            skLineSegment(sketch, "E226.right", {"start": v(51.24, 50.8) * mm, "end": v(51.24, 4.76) * mm});
            skLineSegment(sketch, "E227", {"start": v(-810.7, -4.76) * mm, "end": v(-807.58, -4.76) * mm});
            skLineSegment(sketch, "E228.bottom", {"start": v(-799.71, -21.32) * mm, "end": v(-797.48, -21.32) * mm});
            skLineSegment(sketch, "E228.left", {"start": v(-799.71, -21.32) * mm, "end": v(-799.71, -4.76) * mm});
            skLineSegment(sketch, "E228.right", {"start": v(-797.48, -21.32) * mm, "end": v(-797.48, -4.76) * mm});
            skLineSegment(sketch, "E229.bottom", {"start": v(-668.6, -22.8) * mm, "end": v(-807.58, -22.8) * mm});
            skLineSegment(sketch, "E229.top", {"start": v(-668.6, -23.56) * mm, "end": v(-807.58, -23.56) * mm});
            skLineSegment(sketch, "E229.left", {"start": v(-668.6, -22.8) * mm, "end": v(-668.6, -23.56) * mm});
            skLineSegment(sketch, "E229.right", {"start": v(-807.58, -22.8) * mm, "end": v(-807.58, -23.56) * mm});
            skLineSegment(sketch, "E230.bottom", {"start": v(-807.58, -23.56) * mm, "end": v(-806.67, -23.56) * mm});
            skLineSegment(sketch, "E230.top", {"start": v(-807.58, -4.76) * mm, "end": v(-806.67, -4.76) * mm});
            skLineSegment(sketch, "E230.left", {"start": v(-807.58, -23.56) * mm, "end": v(-807.58, -4.76) * mm});
            skLineSegment(sketch, "E230.right", {"start": v(-806.67, -23.56) * mm, "end": v(-806.67, -4.76) * mm});
            skLineSegment(sketch, "E231.trimOffspring", {"start": v(-797.48, -4.76) * mm, "end": v(140.14, -4.76) * mm});
            skSolve(sketch);
        }
        {
            var Q0;
            Q0 = qSketchRegion(id + "F2", true);
            extrude(context, id + "F3", {"entities" : qUnion([Q0]), "depth" : 3.8 * mm, "offsetDistance" : 25.4 * mm});
        }
        {
            var Q0;
            Q0=makeQuery(id+"F3.opExtrude","CAP_FACE",FACE,{"disambiguationData":[OSD([sQuery(id+"F2.wireOp",EDGE,"E121.bottom"),sQuery(id+"F2.wireOp",EDGE,"E121.top"),sQuery(id+"F2.wireOp",EDGE,"E121.left"),sQuery(id+"F2.wireOp",EDGE,"E121.right"),sQuery(id+"F2.wireOp",EDGE,"E124.left"),sQuery(id+"F2.wireOp",EDGE,"E124.right"),sQuery(id+"F2.wireOp",EDGE,"E125"),sQuery(id+"F2.wireOp",EDGE,"E126"),sQuery(id+"F2.wireOp",EDGE,"E127"),sQuery(id+"F2.wireOp",EDGE,"E128"),sQuery(id+"F2.wireOp",EDGE,"E129"),sQuery(id+"F2.wireOp",EDGE,"E132.bottom"),sQuery(id+"F2.wireOp",EDGE,"E132.top"),sQuery(id+"F2.wireOp",EDGE,"E132.left"),sQuery(id+"F2.wireOp",EDGE,"E132.right"),sQuery(id+"F2.wireOp",EDGE,"E134.left"),sQuery(id+"F2.wireOp",EDGE,"E134.right"),sQuery(id+"F2.wireOp",EDGE,"E135.left"),sQuery(id+"F2.wireOp",EDGE,"E135.right"),sQuery(id+"F2.wireOp",EDGE,"E136.bottom"),sQuery(id+"F2.wireOp",EDGE,"E136.top"),sQuery(id+"F2.wireOp",EDGE,"E136.left"),sQuery(id+"F2.wireOp",EDGE,"E136.right"),sQuery(id+"F2.wireOp",EDGE,"E137.bottom"),sQuery(id+"F2.wireOp",EDGE,"E137.top"),sQuery(id+"F2.wireOp",EDGE,"E137.left"),sQuery(id+"F2.wireOp",EDGE,"E137.right"),sQuery(id+"F2.wireOp",EDGE,"E140.top"),sQuery(id+"F2.wireOp",EDGE,"E140.right"),sQuery(id+"F2.wireOp",EDGE,"E141.bottom"),sQuery(id+"F2.wireOp",EDGE,"E141.top"),sQuery(id+"F2.wireOp",EDGE,"E141.left"),sQuery(id+"F2.wireOp",EDGE,"E141.right"),sQuery(id+"F2.wireOp",EDGE,"E144.bottom"),sQuery(id+"F2.wireOp",EDGE,"E144.top"),sQuery(id+"F2.wireOp",EDGE,"E144.left"),sQuery(id+"F2.wireOp",EDGE,"E145.trimOffspring"),sQuery(id+"F2.wireOp",EDGE,"E146.left"),sQuery(id+"F2.wireOp",EDGE,"E146.right"),sQuery(id+"F2.wireOp",EDGE,"E147.bottom"),sQuery(id+"F2.wireOp",EDGE,"E147.top"),sQuery(id+"F2.wireOp",EDGE,"E148.top"),sQuery(id+"F2.wireOp",EDGE,"E148.left"),sQuery(id+"F2.wireOp",EDGE,"E148.right"),sQuery(id+"F2.wireOp",EDGE,"E149.bottom"),sQuery(id+"F2.wireOp",EDGE,"E149.top"),sQuery(id+"F2.wireOp",EDGE,"E149.right"),sQuery(id+"F2.wireOp",EDGE,"E150.top"),sQuery(id+"F2.wireOp",EDGE,"E150.left"),sQuery(id+"F2.wireOp",EDGE,"E150.right"),sQuery(id+"F2.wireOp",EDGE,"E151.bottom"),sQuery(id+"F2.wireOp",EDGE,"E151.top"),sQuery(id+"F2.wireOp",EDGE,"E152.left"),sQuery(id+"F2.wireOp",EDGE,"E154.trimOffspring"),sQuery(id+"F2.wireOp",EDGE,"E155.top"),sQuery(id+"F2.wireOp",EDGE,"E157.bottom"),sQuery(id+"F2.wireOp",EDGE,"E157.top"),sQuery(id+"F2.wireOp",EDGE,"E158.trimOffspring"),sQuery(id+"F2.wireOp",EDGE,"E160.trimOffspring"),sQuery(id+"F2.wireOp",EDGE,"E166.bottom"),sQuery(id+"F2.wireOp",EDGE,"E166.left"),sQuery(id+"F2.wireOp",EDGE,"E166.right"),sQuery(id+"F2.wireOp",EDGE,"E167.bottom"),sQuery(id+"F2.wireOp",EDGE,"E167.left"),sQuery(id+"F2.wireOp",EDGE,"E167.right"),sQuery(id+"F2.wireOp",EDGE,"E168"),sQuery(id+"F2.wireOp",EDGE,"E169"),sQuery(id+"F2.wireOp",EDGE,"E170"),sQuery(id+"F2.wireOp",EDGE,"E171"),sQuery(id+"F2.wireOp",EDGE,"E173.MirrorCS"),sQuery(id+"F2.wireOp",EDGE,"E174.MirrorCS"),sQuery(id+"F2.wireOp",EDGE,"E175.MirrorCS"),sQuery(id+"F2.wireOp",EDGE,"E176.MirrorCS"),sQuery(id+"F2.wireOp",EDGE,"E177.MirrorCS"),sQuery(id+"F2.wireOp",EDGE,"E178.MirrorCS"),sQuery(id+"F2.wireOp",EDGE,"E179.MirrorCS"),sQuery(id+"F2.wireOp",EDGE,"E180.MirrorCS"),sQuery(id+"F2.wireOp",EDGE,"E181.bottom"),sQuery(id+"F2.wireOp",EDGE,"E181.top"),sQuery(id+"F2.wireOp",EDGE,"E181.left"),sQuery(id+"F2.wireOp",EDGE,"E181.right"),sQuery(id+"F2.wireOp",EDGE,"E182.top"),sQuery(id+"F2.wireOp",EDGE,"E182.left"),sQuery(id+"F2.wireOp",EDGE,"E182.right"),sQuery(id+"F2.wireOp",EDGE,"E185.bottom"),sQuery(id+"F2.wireOp",EDGE,"E185.top"),sQuery(id+"F2.wireOp",EDGE,"E185.left"),sQuery(id+"F2.wireOp",EDGE,"E186.bottom"),sQuery(id+"F2.wireOp",EDGE,"E186.top"),sQuery(id+"F2.wireOp",EDGE,"E186.left"),sQuery(id+"F2.wireOp",EDGE,"E186.right"),sQuery(id+"F2.wireOp",EDGE,"E189"),sQuery(id+"F2.wireOp",EDGE,"E191.trimOffspring"),sQuery(id+"F2.wireOp",EDGE,"E192.trimOffspring"),sQuery(id+"F2.wireOp",EDGE,"E193.bottom"),sQuery(id+"F2.wireOp",EDGE,"E193.left"),sQuery(id+"F2.wireOp",EDGE,"E193.right"),sQuery(id+"F2.wireOp",EDGE,"E194.bottom"),sQuery(id+"F2.wireOp",EDGE,"E194.left"),sQuery(id+"F2.wireOp",EDGE,"E194.right"),sQuery(id+"F2.wireOp",EDGE,"E195.trimOffspring"),sQuery(id+"F2.wireOp",EDGE,"h10VUneO-Nnt3-Yw4C-gTGF-FNu60K5Kcjy2.left"),sQuery(id+"F2.wireOp",EDGE,"h10VUneO-Nnt3-Yw4C-gTGF-FNu60K5Kcjy2.right"),sQuery(id+"F2.wireOp",EDGE,"E159.trimOffspring"),sQuery(id+"F2.wireOp",EDGE,"6wuf6zEC-4NjI-Afmi-R9W3-CMc8OQTcOi21"),sQuery(id+"F2.wireOp",EDGE,"E196"),sQuery(id+"F2.wireOp",EDGE,"E199.bottom"),sQuery(id+"F2.wireOp",EDGE,"E199.left"),sQuery(id+"F2.wireOp",EDGE,"E199.right"),sQuery(id+"F2.wireOp",EDGE,"E200.bottom"),sQuery(id+"F2.wireOp",EDGE,"E200.left"),sQuery(id+"F2.wireOp",EDGE,"E200.right"),sQuery(id+"F2.wireOp",EDGE,"E201"),sQuery(id+"F2.wireOp",EDGE,"E202"),sQuery(id+"F2.wireOp",EDGE,"E204.left"),sQuery(id+"F2.wireOp",EDGE,"E204.right"),sQuery(id+"F2.wireOp",EDGE,"E205"),sQuery(id+"F2.wireOp",EDGE,"E206"),sQuery(id+"F2.wireOp",EDGE,"E207.trimOffspring"),sQuery(id+"F2.wireOp",EDGE,"E208.trimOffspring"),sQuery(id+"F2.wireOp",EDGE,"E209"),sQuery(id+"F2.wireOp",EDGE,"E210"),sQuery(id+"F2.wireOp",EDGE,"E211.trimOffspring"),sQuery(id+"F2.wireOp",EDGE,"E212"),sQuery(id+"F2.wireOp",EDGE,"E213"),sQuery(id+"F2.wireOp",EDGE,"E214"),sQuery(id+"F2.wireOp",EDGE,"E215"),sQuery(id+"F2.wireOp",EDGE,"E216"),sQuery(id+"F2.wireOp",EDGE,"E218.bottom"),sQuery(id+"F2.wireOp",EDGE,"E218.left"),sQuery(id+"F2.wireOp",EDGE,"E218.right"),sQuery(id+"F2.wireOp",EDGE,"E220.bottom"),sQuery(id+"F2.wireOp",EDGE,"E220.top"),sQuery(id+"F2.wireOp",EDGE,"E221.bottom"),sQuery(id+"F2.wireOp",EDGE,"E221.top"),sQuery(id+"F2.wireOp",EDGE,"E221.left"),sQuery(id+"F2.wireOp",EDGE,"E221.right"),sQuery(id+"F2.wireOp",EDGE,"E225.bottom"),sQuery(id+"F2.wireOp",EDGE,"E225.left"),sQuery(id+"F2.wireOp",EDGE,"E225.right"),sQuery(id+"F2.wireOp",EDGE,"E226.bottom"),sQuery(id+"F2.wireOp",EDGE,"E226.left"),sQuery(id+"F2.wireOp",EDGE,"E226.right")])],"isStart":false});
            var sketch = newSketch(context, id + "F4", { "sketchPlane" : qUnion([Q0])});
            skLineSegment(sketch, "E232.top", {"start": v(-914.54, 13.97) * mm, "end": v(-903.8, 13.97) * mm});
            skLineSegment(sketch, "E232.left", {"start": v(-914.54, 23.3) * mm, "end": v(-914.54, 13.97) * mm});
            skLineSegment(sketch, "E232.right", {"start": v(-903.8, 23.3) * mm, "end": v(-903.8, 13.97) * mm});
            skLineSegment(sketch, "E233", {"start": v(-914.54, 23.3) * mm, "end": v(-903.8, 23.3) * mm});
            skPoint(sketch, "E234.orphan", {"position": v(-914.54, 31.38) * mm});
            skLineSegment(sketch, "E235.bottom", {"start": v(-1000.32, 23) * mm, "end": v(-992.7, 23) * mm});
            skLineSegment(sketch, "E235.top", {"start": v(-1000.32, 14.1) * mm, "end": v(-992.7, 14.1) * mm});
            skLineSegment(sketch, "E235.left", {"start": v(-1000.32, 23) * mm, "end": v(-1000.32, 14.1) * mm});
            skLineSegment(sketch, "E235.right", {"start": v(-992.7, 23) * mm, "end": v(-992.7, 14.1) * mm});
            skLineSegment(sketch, "E236.bottom", {"start": v(-1261.94, 5.72) * mm, "end": v(-1026.75, 5.72) * mm});
            skLineSegment(sketch, "E236.top", {"start": v(-1261.94, -5.72) * mm, "end": v(-1032.6, -5.72) * mm});
            skLineSegment(sketch, "E236.left", {"start": v(-1261.94, 5.72) * mm, "end": v(-1261.94, -5.72) * mm});
            skLineSegment(sketch, "E236.right", {"start": v(-1026.75, 5.72) * mm, "end": v(-1026.75, -5.71) * mm});
            skPoint(sketch, "E237", {"position": v(-1261.94, 0) * mm});
            skLineSegment(sketch, "E238", {"start": v(-1032.6, -5.72) * mm, "end": v(-1026.75, -5.71) * mm});
            skSolve(sketch);
        }
        {
            var Q0;
            Q0 = qSketchRegion(id + "F4", true);
            extrude(context, id + "F5", {"entities" : qUnion([Q0]), "depth" : 2.03 * mm, "offsetDistance" : 25.4 * mm});
        }
    });
